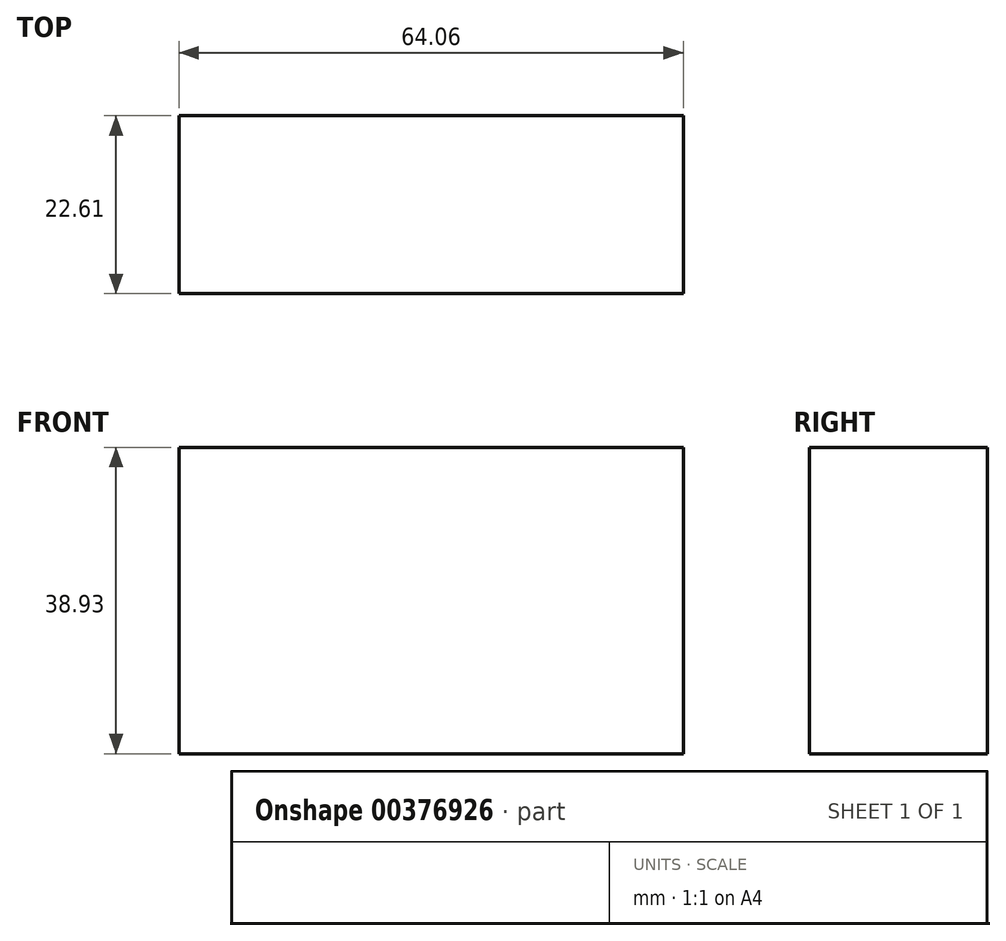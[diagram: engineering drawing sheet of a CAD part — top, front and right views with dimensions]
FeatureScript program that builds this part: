
annotation { "Feature Type Name" : "Feature", "Feature Type Description" : "" }
export const myFeature = defineFeature(function(context is Context, id is Id, definition is map)
    precondition{}
    {
        {
            var Q0;
            Q0=qCreatedBy(makeId("Front.planeOp"),FACE);
            var sketch = newSketch(context, id + "F0", { "sketchPlane" : qUnion([Q0])});
            skLineSegment(sketch, "E0.bottom", {"start": v(21.92, -4.58) * mm, "end": v(-42.14, -4.58) * mm});
            skLineSegment(sketch, "E0.top", {"start": v(21.92, 34.35) * mm, "end": v(-42.14, 34.35) * mm});
            skLineSegment(sketch, "E0.left", {"start": v(21.92, -4.58) * mm, "end": v(21.92, 34.35) * mm});
            skLineSegment(sketch, "E0.right", {"start": v(-42.14, -4.58) * mm, "end": v(-42.14, 34.35) * mm});
            skLineSegment(sketch, "E1.bottom", {"start": v(21.92, 14.88) * mm, "end": v(-42.14, 14.88) * mm});
            skLineSegment(sketch, "E1.top", {"start": v(21.92, 20.54) * mm, "end": v(-42.14, 20.54) * mm});
            skLineSegment(sketch, "E1.left", {"start": v(21.92, 14.88) * mm, "end": v(21.92, 20.54) * mm});
            skLineSegment(sketch, "E1.right", {"start": v(-42.14, 14.88) * mm, "end": v(-42.14, 20.54) * mm});
            skSolve(sketch);
        }
        {
            var Q0;
            Q0 = qSketchRegion(id + "F0", true);
            extrude(context, id + "F1", {"entities" : qUnion([Q0]), "oppositeDirection" : true, "depth" : 22.6 * mm, "offsetDistance" : 25.4 * mm});
        }
    });
